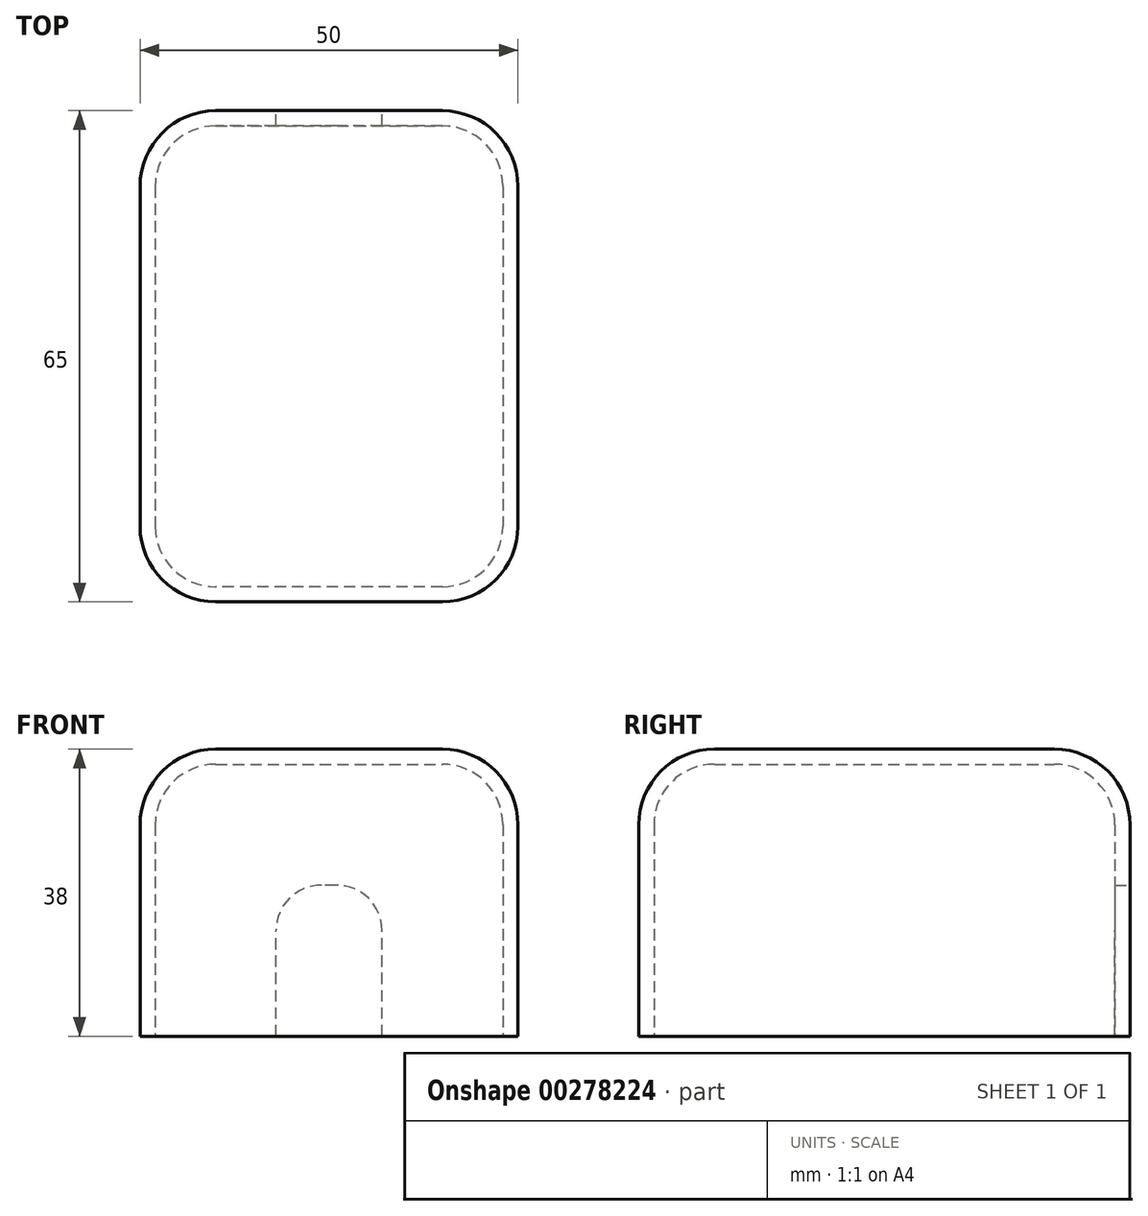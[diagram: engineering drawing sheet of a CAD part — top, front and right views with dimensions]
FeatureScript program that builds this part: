
annotation { "Feature Type Name" : "Feature", "Feature Type Description" : "" }
export const myFeature = defineFeature(function(context is Context, id is Id, definition is map)
    precondition{}
    {
        {
            var Q0;
            Q0=qCreatedBy(makeId("Top.planeOp"),FACE);
            var sketch = newSketch(context, id + "F0", { "sketchPlane" : qUnion([Q0])});
            skLineSegment(sketch, "E0.bottom", {"start": v(25, 32.5) * mm, "end": v(-25, 32.5) * mm});
            skLineSegment(sketch, "E0.top", {"start": v(25, -32.5) * mm, "end": v(-25, -32.5) * mm});
            skLineSegment(sketch, "E0.left", {"start": v(25, 32.5) * mm, "end": v(25, -32.5) * mm});
            skLineSegment(sketch, "E0.right", {"start": v(-25, 32.5) * mm, "end": v(-25, -32.5) * mm});
            skPoint(sketch, "E0.middle", {"position": v(0, 0) * mm});
            skSolve(sketch);
        }
        {
            var Q0;
            Q0 = qSketchRegion(id + "F0", true);
            extrude(context, id + "F1", {"entities" : qUnion([Q0]), "depth" : 38 * mm});
        }
        {
            var Q0;
            Q0=makeQuery(id+"F1.opExtrude","CAP_EDGE",EDGE,{"disambiguationData":[OSD([sQuery(id+"F0.wireOp",EDGE,"E0.bottom")])],"isStart":false});
            var Q1;
            Q1=makeQuery(id+"F1.opExtrude","SWEPT_EDGE",EDGE,{"disambiguationData":[OSD([sQuery(id+"F0.wireOp",EDGE,"E0.bottom"),sQuery(id+"F0.wireOp",EDGE,"E0.left")])]});
            var Q2;
            Q2=makeQuery(id+"F1.opExtrude","CAP_EDGE",EDGE,{"disambiguationData":[OSD([sQuery(id+"F0.wireOp",EDGE,"E0.left")])],"isStart":false});
            var Q3;
            Q3=makeQuery(id+"F1.opExtrude","SWEPT_EDGE",EDGE,{"disambiguationData":[OSD([sQuery(id+"F0.wireOp",EDGE,"E0.top"),sQuery(id+"F0.wireOp",EDGE,"E0.left")])]});
            var Q4;
            Q4=makeQuery(id+"F1.opExtrude","CAP_EDGE",EDGE,{"disambiguationData":[OSD([sQuery(id+"F0.wireOp",EDGE,"E0.top")])],"isStart":false});
            var Q5;
            Q5=makeQuery(id+"F1.opExtrude","CAP_EDGE",EDGE,{"disambiguationData":[OSD([sQuery(id+"F0.wireOp",EDGE,"E0.right")])],"isStart":false});
            var Q6;
            Q6=makeQuery(id+"F1.opExtrude","SWEPT_EDGE",EDGE,{"disambiguationData":[OSD([sQuery(id+"F0.wireOp",EDGE,"E0.bottom"),sQuery(id+"F0.wireOp",EDGE,"E0.right")])]});
            var Q7;
            Q7=makeQuery(id+"F1.opExtrude","SWEPT_EDGE",EDGE,{"disambiguationData":[OSD([sQuery(id+"F0.wireOp",EDGE,"E0.top"),sQuery(id+"F0.wireOp",EDGE,"E0.right")])]});
            fillet(context, id + "F2", {"entities" : qUnion([Q0, Q1, Q2, Q3, Q4, Q5, Q6, Q7]), "radius" : 10 * mm, "tangentPropagation" : true, "allowEdgeOverflow" : false});
        }
        {
            var Q0;
            Q0=makeQuery(id+"F1.opExtrude","CAP_FACE",FACE,{"disambiguationData":[OSD([sQuery(id+"F0.wireOp",EDGE,"E0.bottom"),sQuery(id+"F0.wireOp",EDGE,"E0.top"),sQuery(id+"F0.wireOp",EDGE,"E0.left"),sQuery(id+"F0.wireOp",EDGE,"E0.right")])],"isStart":true});
            shell(context, id + "F3", {"entities" : qUnion([Q0]), "thickness" : 2 * mm});
        }
        {
            var Q0;
            Q0=makeQuery(id+"F1.opExtrude","SWEPT_FACE",FACE,{"disambiguationData":[OSD([sQuery(id+"F0.wireOp",EDGE,"E0.bottom")])]});
            var sketch = newSketch(context, id + "F4", { "sketchPlane" : qUnion([Q0])});
            skLineSegment(sketch, "E1.bottom", {"start": v(7, 20) * mm, "end": v(-7, 20) * mm});
            skLineSegment(sketch, "E1.top", {"start": v(7, -20) * mm, "end": v(-7, -20) * mm});
            skLineSegment(sketch, "E1.left", {"start": v(7, 20) * mm, "end": v(7, -20) * mm});
            skLineSegment(sketch, "E1.right", {"start": v(-7, 20) * mm, "end": v(-7, -20) * mm});
            skPoint(sketch, "E1.middle", {"position": v(0, 0) * mm});
            skSolve(sketch);
        }
        {
            var Q0;
            {var subQ0=sQuery(id+"F4.wireOp",EDGE,"E1.bottom");Q0=makeQuery(id+"F4.imprint","IMPRINT",FACE,{"disambiguationData":[TD([[makeQuery(id+"F4.imprint","IMPRINT",EDGE,{"derivedFrom":subQ0}),1.0]])]});}
            extrude(context, id + "F5", {"entities" : qUnion([Q0]), "operationType" : NewBodyOperationType.REMOVE, "oppositeDirection" : true, "depth" : 25 * mm});
        }
        {
            var Q0;
            Q0=makeQuery(id+"F5.boolean.opBoolean","COPY",EDGE,{"derivedFrom":makeQuery(id+"F5.opExtrude","SWEPT_EDGE",EDGE,{"disambiguationData":[OSD([sQuery(id+"F4.wireOp",EDGE,"E1.bottom"),sQuery(id+"F4.wireOp",EDGE,"E1.right")])]})});
            var Q1;
            Q1=makeQuery(id+"F5.boolean.opBoolean","COPY",EDGE,{"derivedFrom":makeQuery(id+"F5.opExtrude","SWEPT_EDGE",EDGE,{"disambiguationData":[OSD([sQuery(id+"F4.wireOp",EDGE,"E1.bottom"),sQuery(id+"F4.wireOp",EDGE,"E1.left")])]})});
            fillet(context, id + "F6", {"entities" : qUnion([Q0, Q1]), "radius" : 6 * mm, "tangentPropagation" : true, "allowEdgeOverflow" : false});
        }
    });
